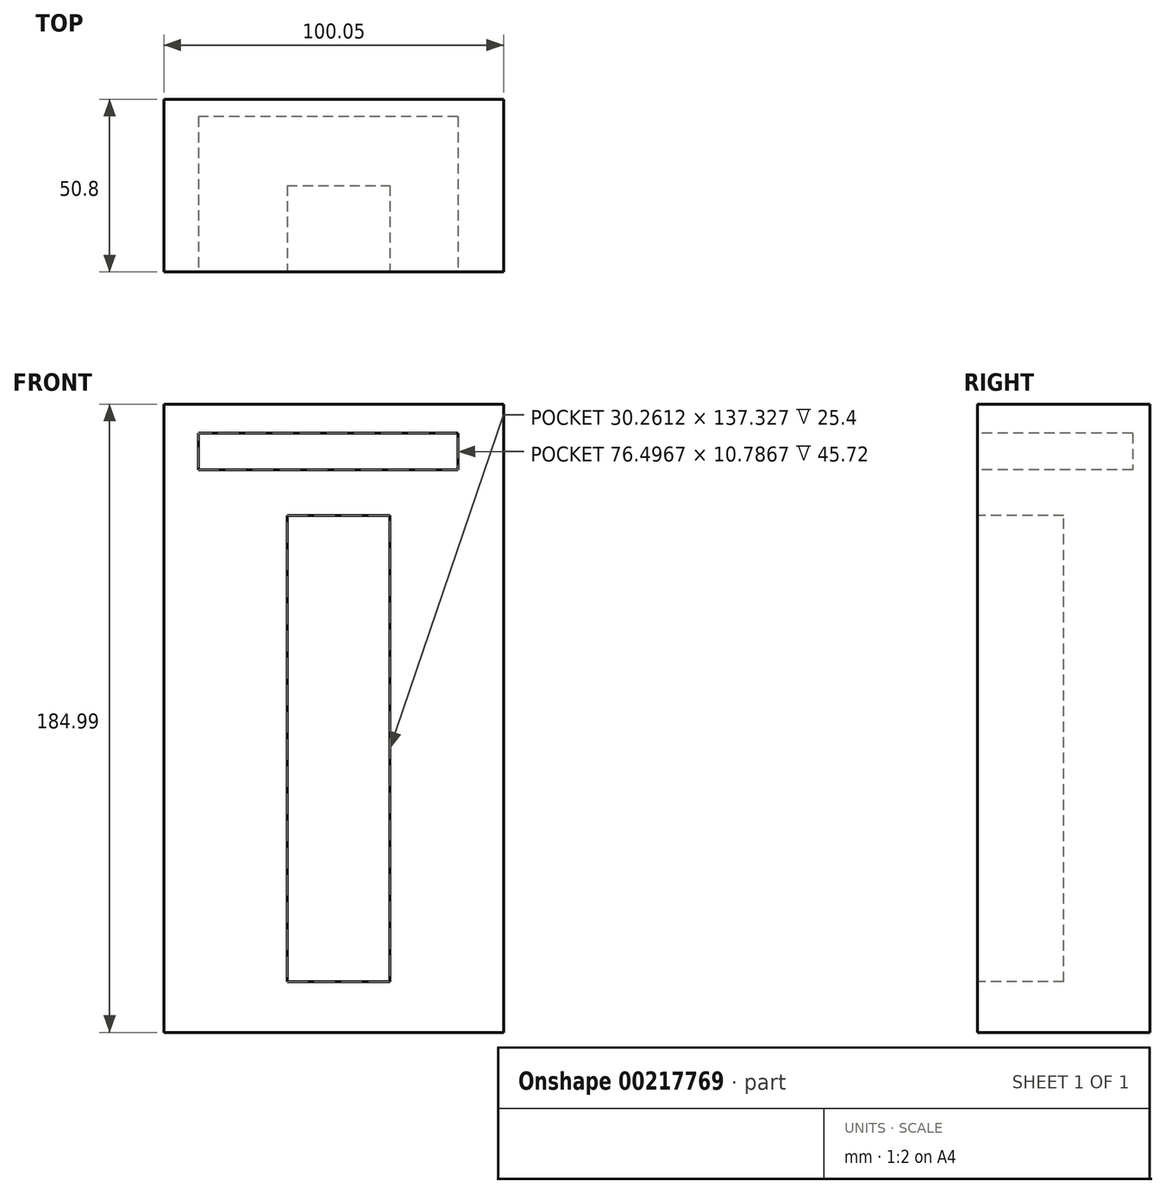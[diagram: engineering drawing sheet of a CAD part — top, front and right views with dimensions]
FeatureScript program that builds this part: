
annotation { "Feature Type Name" : "Feature", "Feature Type Description" : "" }
export const myFeature = defineFeature(function(context is Context, id is Id, definition is map)
    precondition{}
    {
        {
            var Q0;
            Q0=qCreatedBy(makeId("Front.planeOp"),FACE);
            var sketch = newSketch(context, id + "F0", { "sketchPlane" : qUnion([Q0])});
            skLineSegment(sketch, "E0.bottom", {"start": v(-52.75, 74.15) * mm, "end": v(47.3, 74.15) * mm});
            skLineSegment(sketch, "E0.top", {"start": v(-52.75, -110.84) * mm, "end": v(47.3, -110.84) * mm});
            skLineSegment(sketch, "E0.left", {"start": v(-52.75, 74.15) * mm, "end": v(-52.75, -110.84) * mm});
            skLineSegment(sketch, "E0.right", {"start": v(47.3, 74.15) * mm, "end": v(47.3, -110.84) * mm});
            skSolve(sketch);
        }
        {
            var Q0;
            Q0=makeQuery(id+"F0.imprint","IMPRINT",FACE,{"disambiguationData":[TD([[makeQuery(id+"F0.imprint","IMPRINT",EDGE,{"derivedFrom":sQuery(id+"F0.wireOp",EDGE,"E0.bottom")}),-1.0]])]});
            extrude(context, id + "F1", {"entities" : qUnion([Q0]), "depth" : 50.8 * mm});
        }
        {
            var Q0;
            Q0=makeQuery(id+"F1.opExtrude","CAP_FACE",FACE,{"disambiguationData":[OSD([sQuery(id+"F0.wireOp",EDGE,"E0.bottom"),sQuery(id+"F0.wireOp",EDGE,"E0.top"),sQuery(id+"F0.wireOp",EDGE,"E0.left"),sQuery(id+"F0.wireOp",EDGE,"E0.right")])],"isStart":false});
            var sketch = newSketch(context, id + "F2", { "sketchPlane" : qUnion([Q0])});
            skLineSegment(sketch, "E1.bottom", {"start": v(-16.44, -95.93) * mm, "end": v(13.82, -95.93) * mm});
            skLineSegment(sketch, "E1.top", {"start": v(-16.44, 41.4) * mm, "end": v(13.82, 41.4) * mm});
            skLineSegment(sketch, "E1.left", {"start": v(-16.44, -95.93) * mm, "end": v(-16.44, 41.4) * mm});
            skLineSegment(sketch, "E1.right", {"start": v(13.82, -95.93) * mm, "end": v(13.82, 41.4) * mm});
            skSolve(sketch);
        }
        {
            var Q0;
            Q0 = qSketchRegion(id + "F2", true);
            extrude(context, id + "F3", {"entities" : qUnion([Q0]), "operationType" : NewBodyOperationType.REMOVE, "oppositeDirection" : true, "depth" : 25.4 * mm});
        }
        {
            var Q0;
            Q0=makeQuery(id+"F1.opExtrude","CAP_FACE",FACE,{"disambiguationData":[OSD([sQuery(id+"F0.wireOp",EDGE,"E0.bottom"),sQuery(id+"F0.wireOp",EDGE,"E0.top"),sQuery(id+"F0.wireOp",EDGE,"E0.left"),sQuery(id+"F0.wireOp",EDGE,"E0.right")])],"isStart":false});
            var sketch = newSketch(context, id + "F4", { "sketchPlane" : qUnion([Q0])});
            skSolve(sketch);
        }
        {
            var Q0;
            Q0=makeQuery(id+"F4.imprint","IMPRINT",FACE,{"disambiguationData":[TD([[makeQuery(id+"F4.imprint","IMPRINT",EDGE,{"derivedFrom":makeQuery(id+"F1.opExtrude","CAP_EDGE",EDGE,{"disambiguationData":[OSD([sQuery(id+"F0.wireOp",EDGE,"E0.bottom")])],"isStart":false})}),-1.0]])]});
            var sketch = newSketch(context, id + "F5", { "sketchPlane" : qUnion([Q0])});
            skLineSegment(sketch, "E2.bottom", {"start": v(33.89, 65.58) * mm, "end": v(-42.6, 65.58) * mm});
            skLineSegment(sketch, "E2.top", {"start": v(33.89, 54.8) * mm, "end": v(-42.6, 54.8) * mm});
            skLineSegment(sketch, "E2.left", {"start": v(33.89, 65.58) * mm, "end": v(33.89, 54.8) * mm});
            skLineSegment(sketch, "E2.right", {"start": v(-42.6, 65.58) * mm, "end": v(-42.6, 54.8) * mm});
            skSolve(sketch);
        }
        {
            var Q0;
            Q0 = qSketchRegion(id + "F5", true);
            extrude(context, id + "F6", {"entities" : qUnion([Q0]), "operationType" : NewBodyOperationType.REMOVE, "oppositeDirection" : true, "depth" : 45.72 * mm});
        }
        {
            var Q0;
            Q0=qCreatedBy(makeId("Front.planeOp"),FACE);
            var sketch = newSketch(context, id + "F7", { "sketchPlane" : qUnion([Q0])});
            skLineSegment(sketch, "E3.bottom", {"start": v(-136.88, 119.7) * mm, "end": v(163.12, 119.7) * mm});
            skLineSegment(sketch, "E3.top", {"start": v(-136.88, -83.5) * mm, "end": v(163.12, -83.5) * mm});
            skLineSegment(sketch, "E3.left", {"start": v(-136.88, 119.7) * mm, "end": v(-136.88, -83.5) * mm});
            skLineSegment(sketch, "E3.right", {"start": v(163.12, 119.7) * mm, "end": v(163.12, -83.5) * mm});
            skLineSegment(sketch, "E4.bottom", {"start": v(-63.08, 76.2) * mm, "end": v(89.32, 76.2) * mm});
            skLineSegment(sketch, "E4.top", {"start": v(-63.08, 0) * mm, "end": v(89.32, 0) * mm});
            skLineSegment(sketch, "E4.left", {"start": v(-63.08, 76.2) * mm, "end": v(-63.08, 0) * mm});
            skLineSegment(sketch, "E4.right", {"start": v(89.32, 76.2) * mm, "end": v(89.32, 0) * mm});
            skLineSegment(sketch, "E5", {"start": v(13.12, 119.7) * mm, "end": v(13.12, -83.5) * mm, "construction": true});
            skLineSegment(sketch, "E6", {"start": v(13.12, 76.2) * mm, "end": v(13.12, 0) * mm, "construction": true});
            skSolve(sketch);
        }
    });
